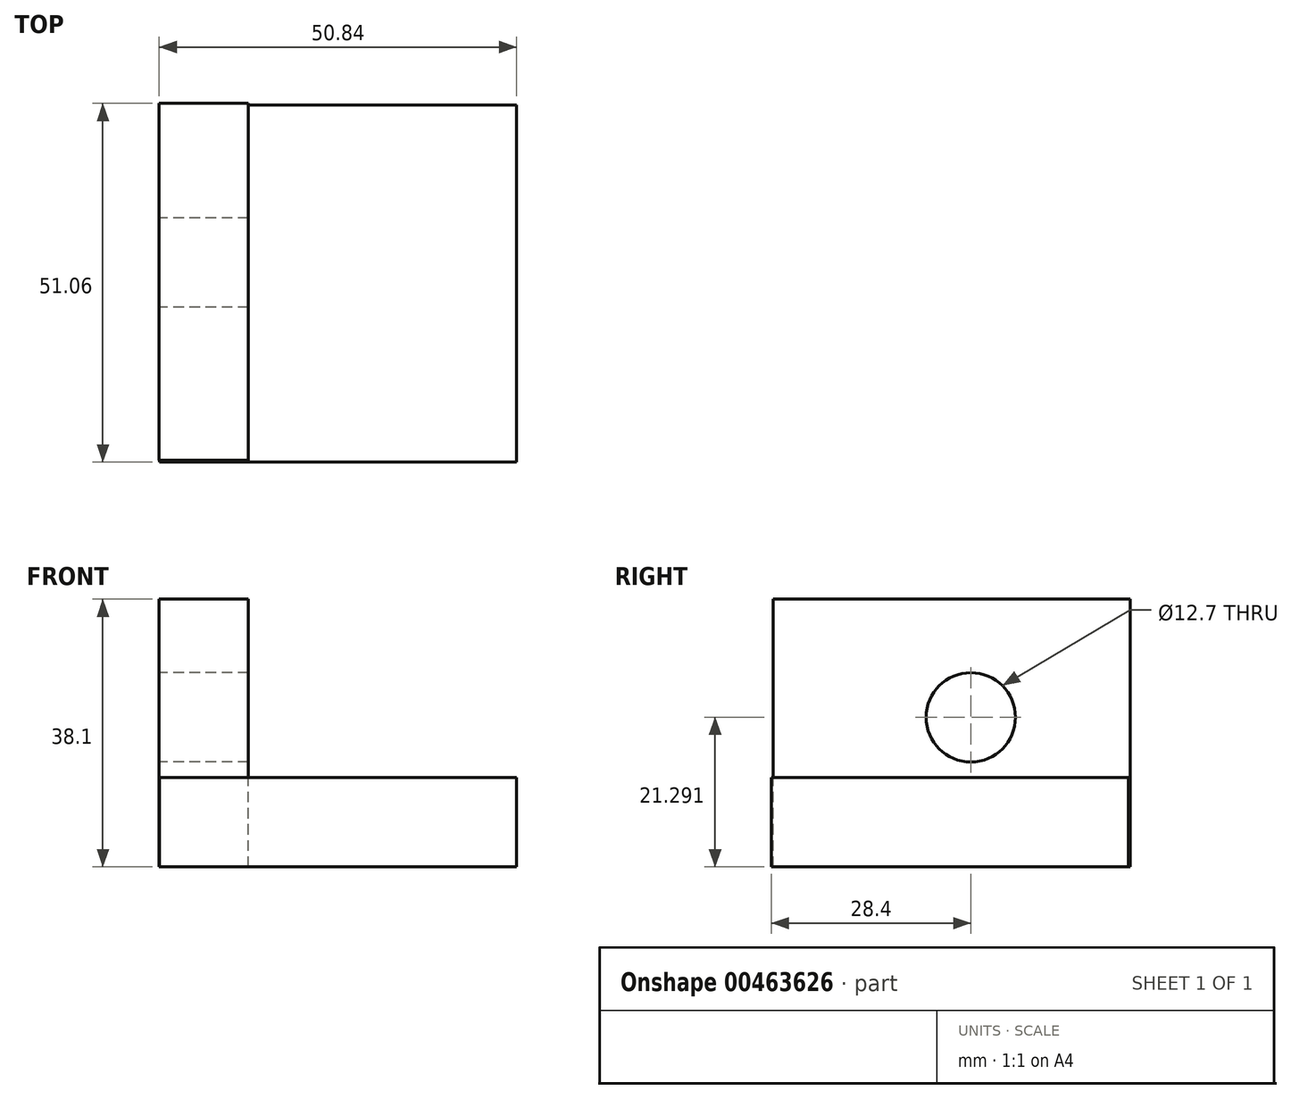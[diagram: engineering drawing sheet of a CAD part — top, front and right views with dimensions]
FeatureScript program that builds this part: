
annotation { "Feature Type Name" : "Feature", "Feature Type Description" : "" }
export const myFeature = defineFeature(function(context is Context, id is Id, definition is map)
    precondition{}
    {
        {
            var Q0;
            Q0=qCreatedBy(makeId("Top.planeOp"),FACE);
            var sketch = newSketch(context, id + "F0", { "sketchPlane" : qUnion([Q0])});
            skLineSegment(sketch, "E0.bottom", {"start": v(-25, 22.4) * mm, "end": v(25.8, 22.4) * mm});
            skLineSegment(sketch, "E0.top", {"start": v(-25, -28.4) * mm, "end": v(25.8, -28.4) * mm});
            skLineSegment(sketch, "E0.left", {"start": v(-25, 22.4) * mm, "end": v(-25, -28.4) * mm});
            skLineSegment(sketch, "E0.right", {"start": v(25.8, 22.4) * mm, "end": v(25.8, -28.4) * mm});
            skSolve(sketch);
        }
        {
            var Q0;
            Q0 = qSketchRegion(id + "F0", true);
            extrude(context, id + "F1", {"entities" : qUnion([Q0]), "depth" : 12.7 * mm});
        }
        {
            var Q0;
            Q0=qCreatedBy(makeId("Top.planeOp"),FACE);
            var sketch = newSketch(context, id + "F2", { "sketchPlane" : qUnion([Q0])});
            skLineSegment(sketch, "E1.bottom", {"start": v(-25.03, -28.14) * mm, "end": v(-12.33, -28.14) * mm});
            skLineSegment(sketch, "E1.top", {"start": v(-25.03, 22.66) * mm, "end": v(-12.33, 22.66) * mm});
            skLineSegment(sketch, "E1.left", {"start": v(-25.03, -28.14) * mm, "end": v(-25.03, 22.66) * mm});
            skLineSegment(sketch, "E1.right", {"start": v(-12.33, -28.14) * mm, "end": v(-12.33, 22.66) * mm});
            skSolve(sketch);
        }
        {
            var Q0;
            Q0 = qSketchRegion(id + "F2", true);
            extrude(context, id + "F3", {"entities" : qUnion([Q0]), "operationType" : NewBodyOperationType.ADD, "depth" : 38.1 * mm});
        }
        {
            var Q0;
            Q0=makeQuery(id+"F3.opExtrude","SWEPT_FACE",FACE,{"disambiguationData":[OSD([sQuery(id+"F2.wireOp",EDGE,"E1.left")])]});
            var sketch = newSketch(context, id + "F4", { "sketchPlane" : qUnion([Q0])});
            skCircle(sketch, "E2", {"center": v(0, 21.3) * mm, "radius": 6.35 * mm});
            skSolve(sketch);
        }
        {
            var Q0;
            Q0=sQuery(id+"F4.wireOp",VERTEX,"E2.center");
            var Q1;
            Q1=makeQuery(id+"F1.opExtrude","SWEPT_BODY",BODY,{"disambiguationData":[OSD([sQuery(id+"F0.wireOp",EDGE,"E0.bottom"),sQuery(id+"F0.wireOp",EDGE,"E0.top"),sQuery(id+"F0.wireOp",EDGE,"E0.left"),sQuery(id+"F0.wireOp",EDGE,"E0.right")])]});
            hole(context, id + "F5", {"style" : HoleStyle.SIMPLE, "endStyle" : HoleEndStyle.THROUGH, "holeDiameter" : 12.7 * mm, "isTappedThrough" : true, "tappedDepth" : 12.7 * mm, "tapClearance" : 3, "locations" : qUnion([Q0]), "scope" : qUnion([Q1])});
        }
    });
